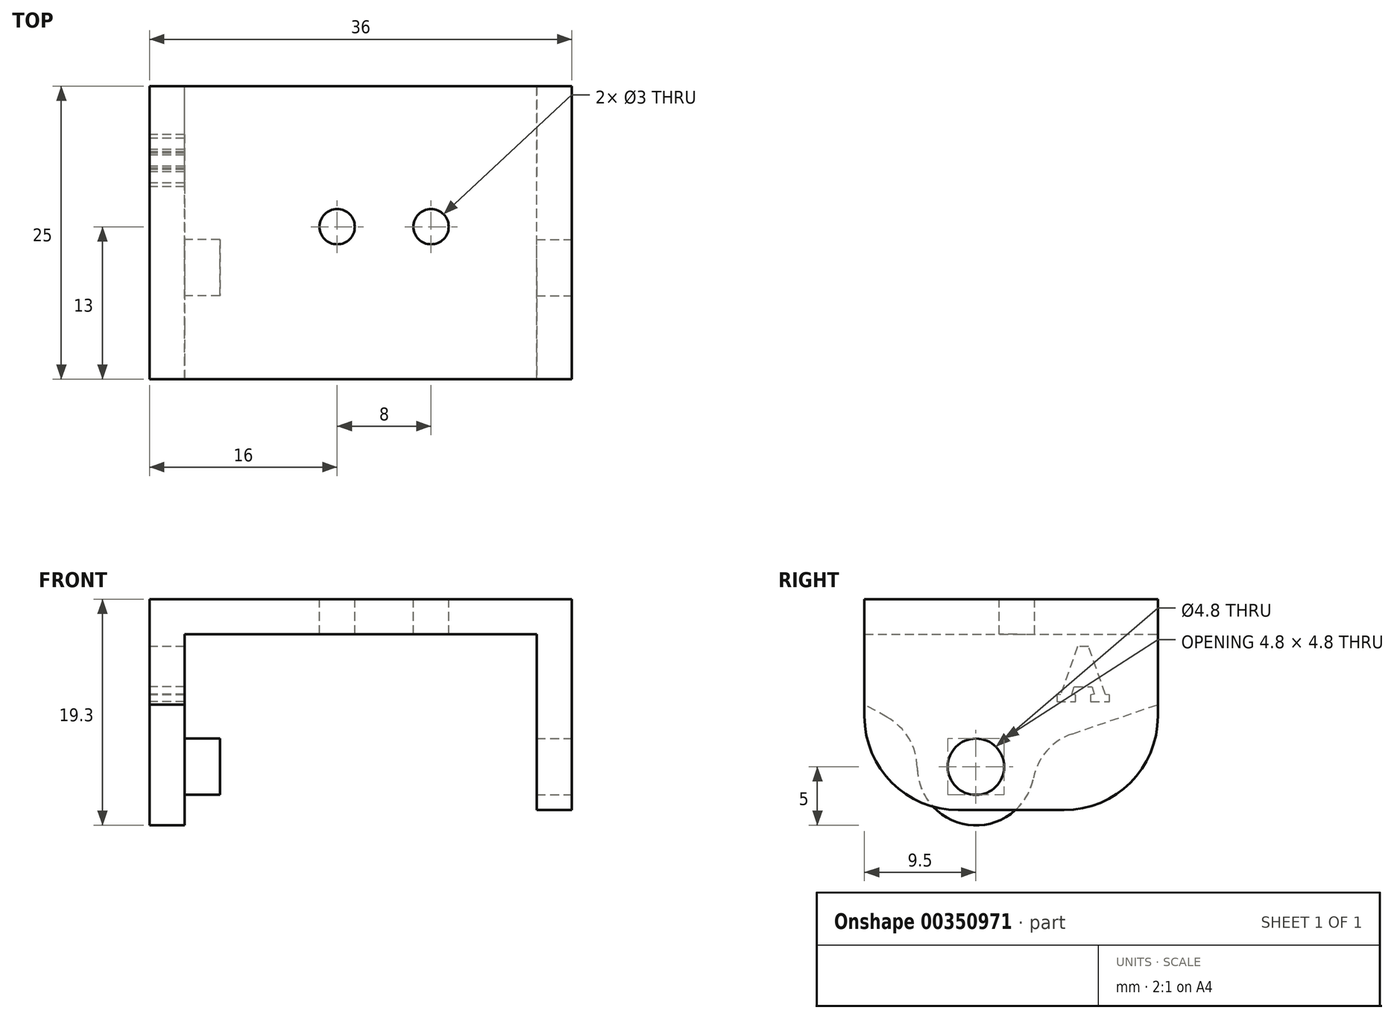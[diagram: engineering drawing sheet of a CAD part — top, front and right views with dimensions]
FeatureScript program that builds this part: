
annotation { "Feature Type Name" : "Feature", "Feature Type Description" : "" }
export const myFeature = defineFeature(function(context is Context, id is Id, definition is map)
    precondition{}
    {
        {
            var Q0;
            Q0=qCreatedBy(makeId("Front.planeOp"),FACE);
            var sketch = newSketch(context, id + "F0", { "sketchPlane" : qUnion([Q0])});
            skLineSegment(sketch, "E0", {"start": v(-16, 0) * mm, "end": v(-16, 18) * mm});
            skLineSegment(sketch, "E1", {"start": v(-16, 18) * mm, "end": v(20, 18) * mm});
            skLineSegment(sketch, "E2", {"start": v(20, 18) * mm, "end": v(20, 0) * mm});
            skLineSegment(sketch, "E3", {"start": v(20, 0) * mm, "end": v(17, 0) * mm});
            skLineSegment(sketch, "E4", {"start": v(17, 0) * mm, "end": v(17, 15) * mm});
            skLineSegment(sketch, "E5", {"start": v(17, 15) * mm, "end": v(-13, 15) * mm});
            skLineSegment(sketch, "E6", {"start": v(-13, 15) * mm, "end": v(-13, 0) * mm});
            skLineSegment(sketch, "E7", {"start": v(-13, 0) * mm, "end": v(-16, 0) * mm});
            skSolve(sketch);
        }
        {
            var Q0;
            Q0=makeQuery(id+"F0.imprint","IMPRINT",FACE,{"disambiguationData":[TD([[makeQuery(id+"F0.imprint","IMPRINT",EDGE,{"derivedFrom":sQuery(id+"F0.wireOp",EDGE,"E0")}),-1.0]])]});
            extrude(context, id + "F1", {"entities" : qUnion([Q0]), "depth" : 25 * mm});
        }
        {
            var Q0;
            Q0=makeQuery(id+"F1.opExtrude","SWEPT_FACE",FACE,{"disambiguationData":[OSD([sQuery(id+"F0.wireOp",EDGE,"E2")])]});
            var sketch = newSketch(context, id + "F2", { "sketchPlane" : qUnion([Q0])});
            skCircle(sketch, "E8", {"center": v(-15.5, 3.7) * mm, "radius": 2.4 * mm});
            skSolve(sketch);
        }
        {
            var Q0;
            Q0=makeQuery(id+"F2.imprint","IMPRINT",FACE,{"disambiguationData":[TD([[makeQuery(id+"F2.imprint","IMPRINT",EDGE,{"derivedFrom":sQuery(id+"F2.wireOp",EDGE,"E8")}),1.0]])]});
            extrude(context, id + "F3", {"entities" : qUnion([Q0]), "operationType" : NewBodyOperationType.REMOVE, "oppositeDirection" : true, "depth" : 50 * mm});
        }
        {
            var Q0;
            Q0=makeQuery(id+"F1.opExtrude","CAP_EDGE",EDGE,{"disambiguationData":[OSD([sQuery(id+"F0.wireOp",EDGE,"E3")])],"isStart":false});
            var Q1;
            Q1=makeQuery(id+"F1.opExtrude","CAP_EDGE",EDGE,{"disambiguationData":[OSD([sQuery(id+"F0.wireOp",EDGE,"E3")])],"isStart":true});
            fillet(context, id + "F4", {"entities" : qUnion([Q0, Q1]), "radius" : 8 * mm, "tangentPropagation" : true, "allowEdgeOverflow" : false});
        }
        {
            var Q0;
            Q0=makeQuery(id+"F1.opExtrude","SWEPT_FACE",FACE,{"disambiguationData":[OSD([sQuery(id+"F0.wireOp",EDGE,"E1")])]});
            var sketch = newSketch(context, id + "F5", { "sketchPlane" : qUnion([Q0])});
            skCircle(sketch, "E9", {"center": v(0, -12) * mm, "radius": 1.5 * mm});
            skCircle(sketch, "E10", {"center": v(8, -12) * mm, "radius": 1.5 * mm});
            skSolve(sketch);
        }
        {
            var Q0;
            Q0=makeQuery(id+"F5.imprint","IMPRINT",FACE,{"disambiguationData":[TD([[makeQuery(id+"F5.imprint","IMPRINT",EDGE,{"derivedFrom":sQuery(id+"F5.wireOp",EDGE,"E9")}),1.0]])]});
            var Q1;
            Q1=makeQuery(id+"F5.imprint","IMPRINT",FACE,{"disambiguationData":[TD([[makeQuery(id+"F5.imprint","IMPRINT",EDGE,{"derivedFrom":sQuery(id+"F5.wireOp",EDGE,"E10")}),1.0]])]});
            extrude(context, id + "F6", {"entities" : qUnion([Q0, Q1]), "operationType" : NewBodyOperationType.REMOVE, "oppositeDirection" : true, "depth" : 5 * mm});
        }
        {
            var Q0;
            Q0=makeQuery(id+"F1.opExtrude","SWEPT_FACE",FACE,{"disambiguationData":[OSD([sQuery(id+"F0.wireOp",EDGE,"E0")])]});
            var sketch = newSketch(context, id + "F7", { "sketchPlane" : qUnion([Q0])});
            skArc(sketch, "E11", {"start": v(10.77, 5.32) * mm, "mid": v(15.95, -1.28) * mm, "end": v(19.87, 6.14) * mm});
            skLineSegment(sketch, "E12", {"start": v(10.77, 5.32) * mm, "end": v(0, 9) * mm});
            skLineSegment(sketch, "E13", {"start": v(19.87, 6.14) * mm, "end": v(25, 9) * mm});
            skSolve(sketch);
        }
        {
            var Q0;
            {var subQ6=sQuery(id+"F7.wireOp",EDGE,"E12");Q0=makeQuery(id+"F7.imprint","IMPRINT",FACE,{"disambiguationData":[TD([[makeQuery(id+"F7.imprint","IMPRINT",EDGE,{"derivedFrom":subQ6}),1.0]])]});}
            var Q1;
            {var subQ6=sQuery(id+"F7.wireOp",EDGE,"E13");Q1=makeQuery(id+"F7.imprint","IMPRINT",FACE,{"disambiguationData":[TD([[makeQuery(id+"F7.imprint","IMPRINT",EDGE,{"derivedFrom":subQ6}),-1.0]])]});}
            extrude(context, id + "F8", {"entities" : qUnion([Q0, Q1]), "operationType" : NewBodyOperationType.REMOVE, "oppositeDirection" : true, "depth" : 3 * mm});
        }
        {
            var Q0;
            Q0=makeQuery(id+"F1.opExtrude","SWEPT_FACE",FACE,{"disambiguationData":[OSD([sQuery(id+"F0.wireOp",EDGE,"E0")])]});
            var sketch = newSketch(context, id + "F9", { "sketchPlane" : qUnion([Q0])});
            skCircle(sketch, "E14", {"center": v(15.5, 3.7) * mm, "radius": 5 * mm});
            skSolve(sketch);
        }
        {
            var Q0;
            {var subQ1=makeQuery(id+"F1.opExtrude","SWEPT_EDGE",EDGE,{"disambiguationData":[OSD([sQuery(id+"F0.wireOp",EDGE,"E0"),sQuery(id+"F0.wireOp",EDGE,"E7")])]});Q0=makeQuery(id+"F9.imprint","IMPRINT",FACE,{"disambiguationData":[TD([[makeQuery(id+"F9.imprint","IMPRINT",EDGE,{"derivedFrom":subQ1}),1.0]])]});}
            extrude(context, id + "F10", {"entities" : qUnion([Q0]), "operationType" : NewBodyOperationType.ADD, "oppositeDirection" : true, "depth" : 3 * mm});
        }
        {
            var Q0;
            {var subQ0=sQuery(id+"F0.wireOp",EDGE,"E0");Q0=makeQuery(id+"F10.boolean.opBoolean","MERGE",FACE,{"derivedFrom":[makeQuery(id+"F1.opExtrude","SWEPT_FACE",FACE,{"disambiguationData":[OSD([subQ0])]}),makeQuery(id+"F10.opExtrude","CAP_FACE",FACE,{"disambiguationData":[OSD([subQ0,sQuery(id+"F0.wireOp",EDGE,"E7"),sQuery(id+"F9.wireOp",EDGE,"E14")])],"isStart":true})]});}
            var sketch = newSketch(context, id + "F11", { "sketchPlane" : qUnion([Q0])});
            skCircle(sketch, "E15", {"center": v(15.5, 3.7) * mm, "radius": 2.4 * mm});
            skSolve(sketch);
        }
        {
            var Q0;
            Q0=makeQuery(id+"F11.imprint","IMPRINT",FACE,{"disambiguationData":[TD([[makeQuery(id+"F11.imprint","IMPRINT",EDGE,{"derivedFrom":sQuery(id+"F11.wireOp",EDGE,"E15")}),1.0]])]});
            extrude(context, id + "F12", {"entities" : qUnion([Q0]), "operationType" : NewBodyOperationType.ADD, "oppositeDirection" : true, "depth" : 6 * mm});
        }
        {
            var Q0;
            Q0=makeQuery(id+"F8.boolean.opBoolean","COPY",EDGE,{"derivedFrom":makeQuery(id+"F8.opExtrude","SWEPT_EDGE",EDGE,{"disambiguationData":[OSD([sQuery(id+"F7.wireOp",EDGE,"E11"),sQuery(id+"F7.wireOp",EDGE,"E13")])]})});
            var Q1;
            Q1=makeQuery(id+"F8.boolean.opBoolean","COPY",EDGE,{"derivedFrom":makeQuery(id+"F8.opExtrude","SWEPT_EDGE",EDGE,{"disambiguationData":[OSD([sQuery(id+"F7.wireOp",EDGE,"E11"),sQuery(id+"F7.wireOp",EDGE,"E12")])]})});
            fillet(context, id + "F13", {"entities" : qUnion([Q0, Q1]), "radius" : 5 * mm, "tangentPropagation" : true, "allowEdgeOverflow" : false});
        }
        {
            var Q0;
            {var subQ0=sQuery(id+"F0.wireOp",EDGE,"E0");Q0=makeQuery(id+"F12.boolean.opBoolean","MERGE",FACE,{"derivedFrom":[makeQuery(id+"F10.boolean.opBoolean","MERGE",FACE,{"derivedFrom":[makeQuery(id+"F1.opExtrude","SWEPT_FACE",FACE,{"disambiguationData":[OSD([subQ0])]}),makeQuery(id+"F10.opExtrude","CAP_FACE",FACE,{"disambiguationData":[OSD([subQ0,sQuery(id+"F0.wireOp",EDGE,"E7"),sQuery(id+"F9.wireOp",EDGE,"E14")])],"isStart":true})]}),makeQuery(id+"F12.opExtrude","CAP_FACE",FACE,{"disambiguationData":[OSD([sQuery(id+"F11.wireOp",EDGE,"E15")])],"isStart":true})]});}
            var sketch = newSketch(context, id + "F14", { "sketchPlane" : qUnion([Q0])});
            skText(sketch, "E16", { "text": "A", "fontName": "RobotoSlab-Bold.ttf"});
            const initialGuessF14  = {"E16": [0.004, 0.00926, 1, 0, 0.00474]};
            skSetInitialGuess(sketch, initialGuessF14);
            skSolve(sketch);
        }
        {
            var Q0;
            Q0=makeQuery(id+"F14.imprint","IMPRINT",FACE,{"disambiguationData":[TD([[makeQuery(id+"F14.imprint","IMPRINT",EDGE,{"derivedFrom":sQuery(id+"F14.wireOp",EDGE,"E16.sketch_text.stroke-0")}),-1.0]])]});
            var Q1;
            Q1=makeQuery(id+"F14.imprint","IMPRINT",FACE,{"disambiguationData":[TD([[makeQuery(id+"F14.imprint","IMPRINT",EDGE,{"derivedFrom":sQuery(id+"F14.wireOp",EDGE,"E16.sketch_text.stroke-16")}),1.0]])]});
            extrude(context, id + "F15", {"entities" : qUnion([Q0, Q1]), "operationType" : NewBodyOperationType.REMOVE, "oppositeDirection" : true, "depth" : 5 * mm});
        }
    });
